# Revit family: TY-FRB-TY313_Imperial
name_source: partatom
category: Sprinklers
revit_build: Autodesk Revit 2016 (Build: 20150220_1215(x64)
units: mm (PartAtom-declared; Revit-internal decimal feet)

## family parameters
Always vertical = Yes
Cut with Voids When Loaded = No
Maintain Annotation Orientation = No
OmniClass Number = 23.65.70.17.11.24
OmniClass Title = Fire Fighting Sprinkler Heads
Part Type = Normal
Room Calculation Point = No
Round Connector Dimension = Use Diameter
Shared = No
Work Plane-Based = No

## types (22) — shared parameters
COBie = Yes
COBie.Component.Name = Sprinklers:Upright_SIN
COBie.Type = Yes
COBie.Type.AssetType = Fixed
COBie.Type.Category = Pr_70_55_97_84:Sprinklers
COBie.Type.DurationUnit = year
COBie.Type.Manufacturer = Tyco Fire Protection Products
COBie.Type.Material = Bronze
COBie.Type.NominalHeight = 0' - 0"
COBie.Type.NominalLength = 0' - 0"
COBie.Type.NominalWidth = 0' - 0"
COBie.Type.Shape = Cylinder
COBie.Type.WarrantyGuarantorParts = http://tycofsbp.com
Coverage = Standard
Coverage_ = Standard
K-Factor = 5.5493
Manufacturer = Tyco Fire Protection Products
Manufacturer URL = www.tyco-fire.com
Material_ = Bronze
Model = TY-FRB
Nominal Diameter 1 = 1"
Orifice = Standard
Orifice Size = 0"
Outside Diameter 1 = 1"
Response = Quick
Response_ = Quick
SIN No = TY313
Takeout 1 = 2"
Technical Data Sheet No = TFP172
zero-valued in all types: COBie.Type.ReplacementCost, Style Id

## per-type parameters (varying)
| type | COBie.Component.Description | COBie.Type.Colour | COBie.Type.Finish | COBie.Type.ModelNumber | COBie.Type.ModelReference | COBie.Type.Size | COBie.Type.WarrantyDurationLabor | COBie.Type.WarrantyGuarantorLabor | Description | Finish_ | Part No | Temperature Rating |
| Wet Upright_135  57.2°C K80 DN15 NPT Br_77-370-1-135 | TY-FRB Wet Upright  135°F K5.6 1/2 NPT Br | Yellow | Natural Brass | 77-370-1-135 | TY-FRB Wet Upright  135°F K5.6 1/2 NPT Br | 1/2"(DN15) |  |  | TY-FRB Wet Upright_Yellow_135  57.2°C K80 DN15 NPT Br | Natural Brass | 77-370-1-135 | 135 °F |
| Wet Upright_155  68.3°C K80 DN15 NPT Br_77-370-1-155 | TY-FRB Wet Upright  155°F K5.6 1/2 NPT Br | Yellow | Natural Brass | 77-370-1-155 | TY-FRB Wet Upright  155°F K5.6 1/2 NPT Br | 1/2"(DN15) |  |  | TY-FRB Wet Upright_Yellow_155  68.3°C K80 DN15 NPT Br | Natural Brass | 77-370-1-155 | 155 °F |
| Wet Upright_175  79.4°C K80 DN15 NPT Br_77-370-1-175 | TY-FRB Wet Upright  175°F K5.6 1/2 NPT Br | Yellow | Natural Brass | 77-370-1-175 | TY-FRB Wet Upright  175°F K5.6 1/2 NPT Br | 1/2"(DN15) |  |  | TY-FRB Wet Upright_Yellow_175  79.4°C K80 DN15 NPT Br | Natural Brass | 77-370-1-175 | 175 °F |
| Wet Upright_200  93.3°C K80 DN15 NPT Br_77-370-1-200 | TY-FRB Wet Upright  200°F K5.6 1/2 NPT Br | Yellow | Natural Brass | 77-370-1-200 | TY-FRB Wet Upright  200°F K5.6 1/2 NPT Br | 1/2"(DN15) |  |  | TY-FRB Wet Upright_Yellow_200  93.3°C K80 DN15 NPT Br | Natural Brass | 77-370-1-200 | 200 °F |
| Wet Upright_286  141.1°C K80 DN15 NPT Br_77-370-1-286 | TY-FRB Wet Upright  286°F K5.6 1/2 NPT Br | Yellow | Natural Brass | 77-370-1-286 | TY-FRB Wet Upright  286°F K5.6 1/2 NPT Br | 1/2"(DN15) |  |  | TY-FRB Wet Upright_Yellow_286  141.1°C K80 DN15 NPT Br | Natural Brass | 77-370-1-286 | 286 °F |
| Wet Upright_135  57.2°C K80 DN15 NPT Wh9010_77-370-3-135 | TY-FRB Wet Upright  57.2°C K80 DN15 NPT Wh9010 | White | Pure White | 77-370-3-135 | TY-FRB Wet Upright  57.2°C K80 DN15 NPT Wh9010 | 1/2"(DN15) |  |  | TY-FRB Wet Upright_White_135  57.2°C K80 DN15 NPT Wh9010 | White RAL9010 | 77-370-3-135 | 135 °F |
| Wet Upright_155  57.2°C K80 DN15 NPT Wh9010_77-370-3-155 | TY-FRB Wet Upright  68.3°C K80 DN15 NPT Wh9010 | White | Pure White | 77-370-3-155 | TY-FRB Wet Upright  68.3°C K80 DN15 NPT Wh9010 | 1/2'(DN15) |  |  | TY-FRB Wet Upright_White_155  68.3°C K80 DN15 NPT Wh9010 | White RAL9010 | 77-370-3-155 | 155 °F |
| Wet Upright_175  57.2°C K80 DN15 NPT Wh9010_77-370-3-175 | TY-FRB Wet Upright  79.4°C K80 DN15 NPT Wh9010 | White | Pure White | 77-370-3-175 | TY-FRB Wet Upright  79.4°C K80 DN15 NPT Wh9010 | 1/2"(DN15) |  |  | TY-FRB Wet Upright_White_175  79.4°C K80 DN15 NPT Wh9010 | White RAL9010 | 77-370-3-175 | 175 °F |
| Wet Upright_200  57.2°C K80 DN15 NPT Wh9010_77-370-3-200 | TY-FRB Wet Upright  93.3°C K80 DN15 NPT Wh9010 | White | Pure White | 77-370-3-200 | TY-FRB Wet Upright  93.3°C K80 DN15 NPT Wh9010 | 1/2"(DN15) |  |  | TY-FRB Wet Upright_White_200  93.3°C K80 DN15 NPT Wh9010 | White RAL9010 | 77-370-3-200 | 200 °F |
| Wet Upright_286  57.2°C K80 DN15 NPT Wh9010_77-370-3-286 | TY-FRB Wet Upright  141.1°C K80 DN15 NPT Wh9010 | White | Pure White | 77-370-3-286 | TY-FRB Wet Upright  141.1°C K80 DN15 NPT Wh9010 | 1/2"(DN15) |  |  | TY-FRB Wet Upright_White_286  141.1°C K80 DN15 NPT Wh9010 | White RAL9010 | 77-370-3-286 | 286 °F |
| Wet Upright_135  57.2°C K80 DN15 NPT Wh9003_77-370-4-135 | TY-FRB Wet Upright  135°F K5.6 1/2 NPT Wh9003 | White | Signal White | 77-370-4-135 | TY-FRB Wet Upright  135°F K5.6 1/2 NPT Wh9003 | 1/2"(DN15) |  |  | TY-FRB Wet Upright_White_135  57.2°C K80 DN15 NPT Wh9003 | White RAL9003 | 77-370-4-135 | 135 °F |
| Wet Upright_155  68.3°C K80 DN15 NPT Wh9003_77-370-4-155 | TY-FRB Wet Upright  155°F K5.6 1/2 NPT Wh9003 | White | Signal White | 77-370-4-155 | TY-FRB Wet Upright  155°F K5.6 1/2 NPT Wh9003 | 1/2"(DN15) |  |  | TY-FRB Wet Upright_White_155  68.3°C K80 DN15 NPT Wh9003 | White RAL9003 | 77-370-4-155 | 155 °F |
| Wet Upright_White_175  79.4°C K80 DN15 NPT Wh9003_77-370-4-175 | TY-FRB Wet Upright  175°F K5.6 1/2 NPT Wh9003 | White | Signal White | 77-370-4-175 | TY-FRB Wet Upright  175°F K5.6 1/2 NPT Wh9003 | 1/2"(DN15) |  |  | TY-FRB Wet Upright_White_175  79.4°C K80 DN15 NPT Wh9003 | White RAL9003 | 77-370-4-175 | 175 °F |
| Wet Upright_200  93.3°C K80 DN15 NPT Wh9003_77-370-4-200 | TY-FRB Wet Upright  200°F K5.6 1/2 NPT Wh9003 | White | Signal White | 77-370-4-200 | TY-FRB Wet Upright  200°F K5.6 1/2 NPT Wh9003 | 1/2"(DN15) |  |  | TY-FRB Wet Upright_White_200  93.3°C K80 DN15 NPT Wh9003 | White RAL9003 | 77-370-4-200 | 200 °F |
| Wet Upright_286  141.1°C K80 DN15 NPT Wh9003_77-370-4-286 | TY-FRB Wet Upright  286°F K5.6 1/2 NPT Wh9003 | White | Signal White | 77-370-4-286 | TY-FRB Wet Upright  286°F K5.6 1/2 NPT Wh9003 | 1/2"(DN15) |  |  | TY-FRB Wet Upright_White_286  141.1°C K80 DN15 NPT Wh9003 | White RAL9003 | 77-370-4-286 | 286 °F |
| Wet Upright_155   57.2°C K80 DN15 NPT JBlk_77-370-5-155 | TY-FRB Wet Upright  135°F K5.6 1/2 NPT Chr | Black | Jet Black | 77-370-5-155 | TY-FRB Wet Upright  135°F K5.6 1/2 NPT Chr | 1/2"(DN15) |  |  | TY-FRB Wet Upright_Black_155   57.2°C K80 DN15 NPT JBlk | Jet Black RAL9005 | 77-370-5-155 | 135 °F |
| Wet Upright_155   57.2°C K80 DN15 NPT JBlk_77-370-5-200 | TY-FRB Wet Upright_Black_155   135°F K5.6 1/2 NPT Chr | Black | Jet Black | 77-370-5-200 | TY-FRB Wet Upright_Black_155   135°F K5.6 1/2 NPT Chr | 1/2"(DN15) |  |  | TY-FRB Wet Upright_Black_155   57.2°C K80 DN15 NPT JBlk | Jet Black RAL9005 | 77-370-5-200 | 135 °F |
| Wet Upright_135  57.2°C K80 DN15 NPT Chr_77-370-9-135 | TY-FRB Wet Upright  135°F K5.6 1/2 NPT Chr | Silver | Chrome Plated | 77-370-9-135 | TY-FRB Wet Upright  135°F K5.6 1/2 NPT Chr | 1/2"(DN15) |  |  | TY-FRB Wet Upright_Silver_135  57.2°C K80 DN15 NPT Chr | Chrome Plated | 77-370-9-135 | 135 °F |
| Wet Upright_155  68.3°C K80 DN15 NPT Chr_77-370-9-155 | TY-FRB Wet Upright  155°F K5.6 1/2 NPT Chr | Silver | Chrome Plated | 77-370-9-155 | TY-FRB Wet Upright  155°F K5.6 1/2 NPT Chr | 1/2"(DN15) |  |  | TY-FRB Wet Upright_Silver_155  68.3°C K80 DN15 NPT Chr | Chrome Plated | 77-370-9-155 | 155 °F |
| Wet Upright_175  79.4°C K80 DN15 NPT Chr_77-370-9-175 | TY-FRB Wet Upright  175°F K5.6 1/2 NPT Chr | Silver | Chrome Plated | 77-370-9-175 | TY-FRB Wet Upright  175°F K5.6 1/2 NPT Chr | 1/2"(DN15) |  |  | TY-FRB Wet Upright_Silver_175  79.4°C K80 DN15 NPT Chr | Chrome Plated | 77-370-9-175 | 175 °F |
| Wet Upright_200  93.3°C K80 DN15 NPT Chr_77-370-9-200 | TY-FRB Wet Upright  200°F K5.6 1/2 NPT Chr | Silver | Chrome Plated | 77-370-9-200 | TY-FRB Wet Upright  200°F K5.6 1/2 NPT Chr | 1/2"(DN15) | n/ | an/a | TY-FRB Wet Upright_Silver_200  93.3°C K80 DN15 NPT Chr | Chrome Plated | 77-370-9-200 | 200 °F |
| Wet Upright_286  141.1°C K80 DN15 NPT Chr_77-370-9-286 | TY-FRB Wet Upright  286°F K5.6 1/2 NPT Chr | Silver | Chrome Plated | 77-370-9-286 | TY-FRB Wet Upright  286°F K5.6 1/2 NPT Chr | 1/2"(DN15) |  |  | TY-FRB Wet Upright_Silver_286  141.1°C K80 DN15 NPT Chr | Chrome Plated | 77-370-9-286 | 286 °F |

## geometry (parser evidence)
native form markers: Blend x2, Sweep x59
no freeform markers — native parametric forms only
